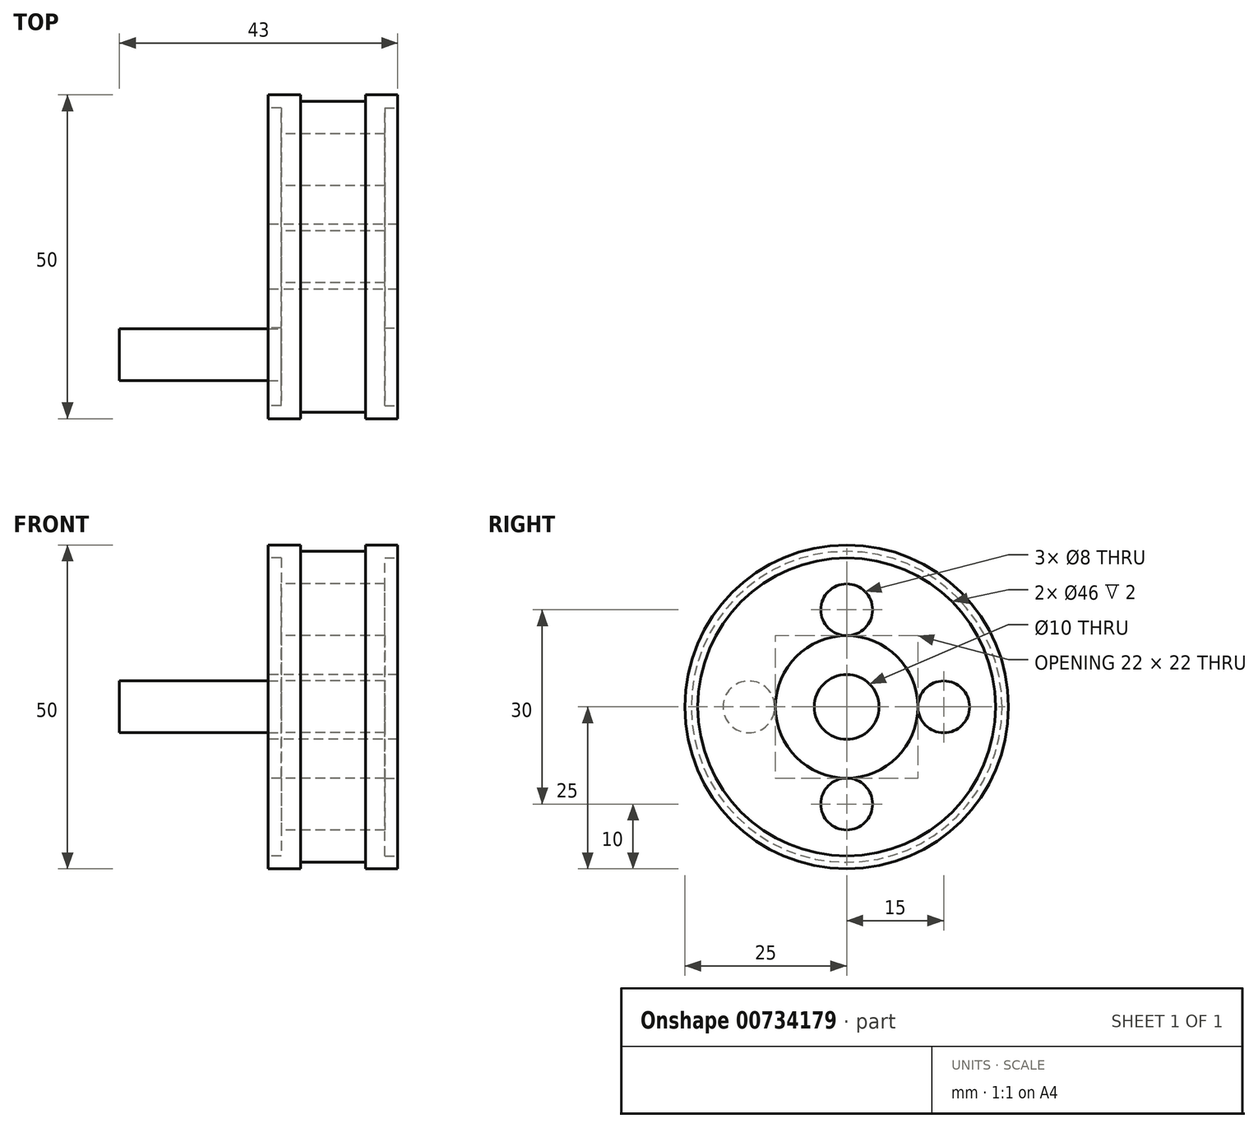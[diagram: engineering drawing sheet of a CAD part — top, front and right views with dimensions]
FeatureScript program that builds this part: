
annotation { "Feature Type Name" : "Feature", "Feature Type Description" : "" }
export const myFeature = defineFeature(function(context is Context, id is Id, definition is map)
    precondition{}
    {
        {
            var Q0;
            Q0=qCreatedBy(makeId("Front.planeOp"),FACE);
            var sketch = newSketch(context, id + "F0", { "sketchPlane" : qUnion([Q0])});
            skLineSegment(sketch, "E0", {"start": v(10.98, 25) * mm, "end": v(5.98, 25) * mm});
            skLineSegment(sketch, "E1", {"start": v(5.98, 25) * mm, "end": v(5.98, 24) * mm});
            skLineSegment(sketch, "E2", {"start": v(5.98, 24) * mm, "end": v(-4.02, 24) * mm});
            skLineSegment(sketch, "E3", {"start": v(-4.02, 24) * mm, "end": v(-4.02, 25) * mm});
            skLineSegment(sketch, "E4", {"start": v(-4.02, 25) * mm, "end": v(-9.02, 25) * mm});
            skLineSegment(sketch, "E5", {"start": v(-14.87, 0) * mm, "end": v(16.95, 0) * mm});
            skLineSegment(sketch, "E6", {"start": v(-9.02, 5) * mm, "end": v(10.98, 5) * mm});
            skLineSegment(sketch, "E7", {"start": v(-9.02, 25) * mm, "end": v(-9.02, 5) * mm});
            skLineSegment(sketch, "E8", {"start": v(10.98, 25) * mm, "end": v(10.98, 5) * mm});
            skSolve(sketch);
        }
        {
            var Q0;
            Q0 = qSketchRegion(id + "F0", true);
            var Q1;
            Q1=sQuery(id+"F0.wireOp",EDGE,"E5");
            revolve(context, id + "F1", {"surfaceOperationType" : NewSurfaceOperationType.NEW, "entities" : qUnion([Q0]), "axis" : qUnion([Q1]), "revolveType" : RevolveType.FULL});
        }
        {
            var Q0;
            Q0=makeQuery(id+"F1.opRevolve","SWEPT_FACE",FACE,{"disambiguationData":[OSD([sQuery(id+"F0.wireOp",EDGE,"E7")])]});
            var sketch = newSketch(context, id + "F2", { "sketchPlane" : qUnion([Q0])});
            skCircle(sketch, "E9", {"center": v(0, 15) * mm, "radius": 4 * mm});
            skCircle(sketch, "E10.1.0", {"center": v(-15, 0) * mm, "radius": 4 * mm});
            skCircle(sketch, "E10.2.0", {"center": v(0, -15) * mm, "radius": 4 * mm});
            skCircle(sketch, "E10.3.0", {"center": v(15, 0) * mm, "radius": 4 * mm});
            skPoint(sketch, "E10.center", {"position": v(0, 0) * mm});
            skSolve(sketch);
        }
        {
            var Q0;
            Q0=makeQuery(id+"F2.imprint","IMPRINT",FACE,{"disambiguationData":[TD([[makeQuery(id+"F2.imprint","IMPRINT",EDGE,{"derivedFrom":sQuery(id+"F2.wireOp",EDGE,"E9")}),1.0]])]});
            var Q1;
            Q1=makeQuery(id+"F2.imprint","IMPRINT",FACE,{"disambiguationData":[TD([[makeQuery(id+"F2.imprint","IMPRINT",EDGE,{"derivedFrom":sQuery(id+"F2.wireOp",EDGE,"E10.1.0")}),1.0]])]});
            var Q2;
            Q2=makeQuery(id+"F2.imprint","IMPRINT",FACE,{"disambiguationData":[TD([[makeQuery(id+"F2.imprint","IMPRINT",EDGE,{"derivedFrom":sQuery(id+"F2.wireOp",EDGE,"E10.2.0")}),1.0]])]});
            extrude(context, id + "F3", {"entities" : qUnion([Q0, Q1, Q2]), "operationType" : NewBodyOperationType.REMOVE, "endBound" : BoundingType.THROUGH_ALL, "oppositeDirection" : true, "depth" : 25 * mm, "offsetDistance" : 25 * mm});
        }
        {
            var Q0;
            Q0=makeQuery(id+"F2.imprint","IMPRINT",FACE,{"disambiguationData":[TD([[makeQuery(id+"F2.imprint","IMPRINT",EDGE,{"derivedFrom":sQuery(id+"F2.wireOp",EDGE,"E9")}),-1.0]])]});
            cPlane(context, id + "F4", {"entities" : qUnion([Q0]), "cplaneType" : CPlaneType.OFFSET, "offset" : 1 * mm, "width" : 150 * mm, "height" : 150 * mm});
        }
        {
            var Q0;
            Q0=qCreatedBy(id+"F4.planeOp",FACE);
            var sketch = newSketch(context, id + "F5", { "sketchPlane" : qUnion([Q0])});
            skCircle(sketch, "E11", {"center": v(0, 0) * mm, "radius": 23 * mm});
            skCircle(sketch, "E12", {"center": v(0, 0) * mm, "radius": 11 * mm});
            skSolve(sketch);
        }
        {
            var Q0;
            Q0 = qSketchRegion(id + "F5", true);
            extrude(context, id + "F6", {"entities" : qUnion([Q0]), "operationType" : NewBodyOperationType.REMOVE, "oppositeDirection" : true, "depth" : 3 * mm, "offsetDistance" : 25 * mm});
        }
        {
            var Q0;
            Q0=makeQuery(id+"F1.opRevolve","SWEPT_FACE",FACE,{"disambiguationData":[OSD([sQuery(id+"F0.wireOp",EDGE,"E8")])]});
            cPlane(context, id + "F7", {"entities" : qUnion([Q0]), "cplaneType" : CPlaneType.OFFSET, "offset" : 1 * mm, "width" : 150 * mm, "height" : 150 * mm});
        }
        {
            var Q0;
            Q0=qCreatedBy(id+"F7.planeOp",FACE);
            var sketch = newSketch(context, id + "F8", { "sketchPlane" : qUnion([Q0])});
            skCircle(sketch, "E13", {"center": v(0, 0) * mm, "radius": 23 * mm});
            skCircle(sketch, "E14", {"center": v(0, 0) * mm, "radius": 11 * mm});
            skSolve(sketch);
        }
        {
            var Q0;
            Q0 = qSketchRegion(id + "F8", true);
            extrude(context, id + "F9", {"entities" : qUnion([Q0]), "operationType" : NewBodyOperationType.REMOVE, "oppositeDirection" : true, "depth" : 3 * mm, "offsetDistance" : 25 * mm});
        }
        {
            var Q0;
            Q0=makeQuery(id+"F6.boolean.opBoolean","COPY",FACE,{"derivedFrom":makeQuery(id+"F6.opExtrude","CAP_FACE",FACE,{"disambiguationData":[OSD([sQuery(id+"F5.wireOp",EDGE,"E11"),sQuery(id+"F5.wireOp",EDGE,"E12")])],"isStart":false})});
            var sketch = newSketch(context, id + "F10", { "sketchPlane" : qUnion([Q0])});
            skCircle(sketch, "E15", {"center": v(15.1, 0) * mm, "radius": 4 * mm});
            skSolve(sketch);
        }
        {
            var Q0;
            Q0 = qSketchRegion(id + "F10", true);
            extrude(context, id + "F11", {"entities" : qUnion([Q0]), "operationType" : NewBodyOperationType.ADD, "depth" : 25 * mm, "offsetDistance" : 25 * mm});
        }
    });
